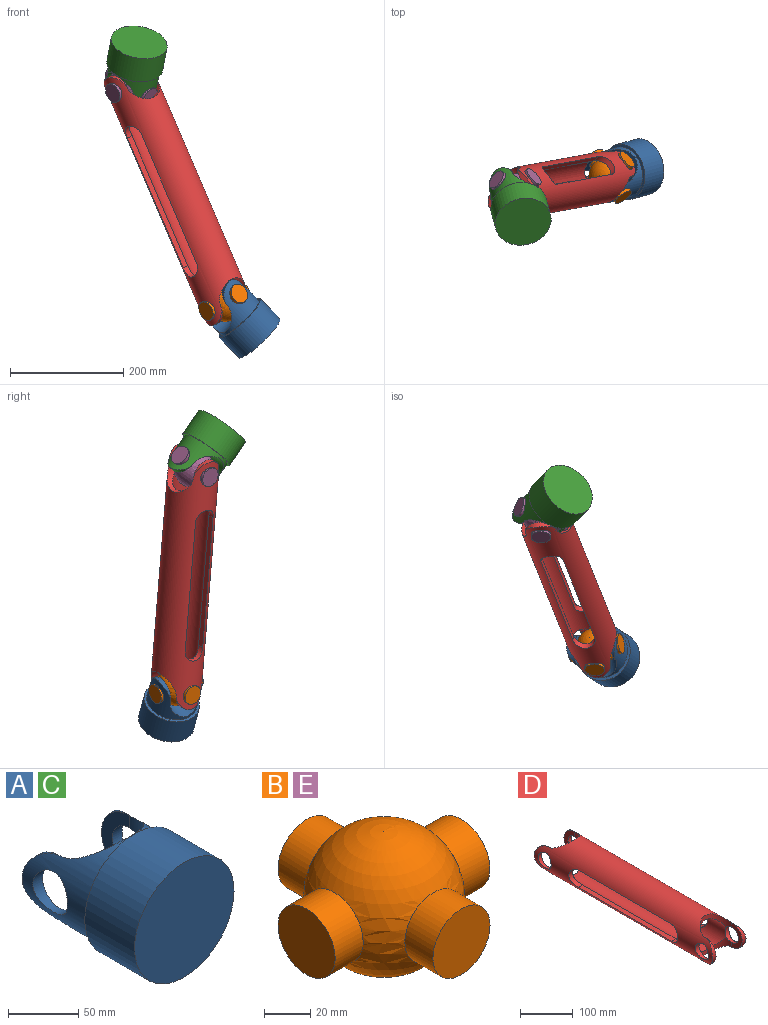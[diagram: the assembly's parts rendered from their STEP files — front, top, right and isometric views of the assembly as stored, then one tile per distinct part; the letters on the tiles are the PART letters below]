
ASSEMBLY  parts=5 mates=4
PART A: 11 faces, bbox 100x118.3x100 mm
  f0: cylinder r=45mm len=90mm, axis (0,-1,0), area 7768.4mm2, adj f4,f6,f7,f8,f9,f10
  f1: plane 56.57x28.28mm, normal (-1,0,0), area 775.6mm2, adj f6,f9,f10
  f2: plane 56.57x28.28mm, normal (1,0,0), area 775.6mm2, adj f6,f7,f8
  f3: cylinder r=50mm len=100mm, axis (0,-1,0), area 15708mm2, adj f4,f5
  f4: plane 100x100mm, normal (0,1,0), area 1492.3mm2, adj f0,f3
  f5: plane 100x100mm, normal (0,-1,0), area 7854mm2, adj f3
  f6: cylinder r=35mm len=90mm, axis (0,0,1), area 7167.4mm2, adj f0,f1,f2,f8,f10
  f7: cylinder r=28.28mm len=56.57mm, axis (1,0,0), area 458.2mm2, adj f0,f2
  f8: cylinder r=17.5mm len=35mm, axis (1,0,0), area 1033.1mm2, adj f0,f2,f6
  f9: cylinder r=28.28mm len=56.57mm, axis (1,0,0), area 458.1mm2, adj f0,f1
  f10: cylinder r=17.5mm len=35mm, axis (1,0,0), area 1033.8mm2, adj f0,f1,f6
PART B: 9 faces, bbox 95x95x70 mm
  f0: sphere r=35mm, area 11269mm2, adj f1,f4,f6,f7
  f1: cylinder r=17.5mm len=35mm, axis (0,1,0), area 1890mm2, adj f0,f2
  f2: plane 35x35mm, normal (0,1,0), area 962.1mm2, adj f1
  f3: plane 35x35mm, normal (0,-1,0), area 962.1mm2, adj f4
  f4: cylinder r=17.5mm len=35mm, axis (0,1,0), area 1890mm2, adj f0,f3
  f5: plane 35x35mm, normal (1,0,0), area 962.1mm2, adj f6
  f6: cylinder r=17.5mm len=35mm, axis (-1,0,0), area 1890mm2, adj f0,f5
  f7: cylinder r=17.5mm len=35mm, axis (-1,0,0), area 1890mm2, adj f0,f8
  f8: plane 35x35mm, normal (-1,0,0), area 962.1mm2, adj f7
PART C: same geometry as A
PART D: 26 faces, bbox 90x476.6x90 mm
  f0: cylinder r=45mm len=476.57mm, axis (0,1,0), area 88359.1mm2, adj f2,f3,f6,f7,f8,f9,f10,f11
  f1: cylinder r=35mm len=395.25mm, axis (0,1,0), area 57669.8mm2, adj f2,f3,f6,f7,f8,f9,f10,f11
  f2: cylinder r=35mm len=70mm, axis (0,0,1), area 1388.1mm2, adj f0,f1,f20,f21,f22,f23
  f3: cylinder r=35mm len=70mm, axis (0,0,1), area 1388.1mm2, adj f0,f1,f20,f21,f22,f23
  f4: plane 56.57x28.28mm, normal (-1,0,0), area 775.6mm2, adj f14,f15,f17,f19
  f5: plane 56.57x28.28mm, normal (1,0,0), area 775.6mm2, adj f14,f15,f16,f18
  f6: plane 250x11.59mm, normal (0,0,1), area 2897.1mm2, adj f0,f1,f7,f9
  f7: cylinder r=20mm len=40mm, axis (-1,0,0), area 675.4mm2, adj f0,f1,f6,f8
  f8: plane 250x11.59mm, normal (0,0,-1), area 2897.1mm2, adj f0,f1,f7,f9
  f9: cylinder r=20mm len=40mm, axis (-1,0,0), area 675.4mm2, adj f0,f1,f6,f8
  f10: cylinder r=20mm len=40mm, axis (-1,0,0), area 675.4mm2, adj f0,f1,f11,f13
  f11: plane 250x11.59mm, normal (0,0,-1), area 2897.1mm2, adj f0,f1,f10,f12
  f12: cylinder r=20mm len=40mm, axis (-1,0,0), area 675.4mm2, adj f0,f1,f11,f13
  f13: plane 250x11.59mm, normal (0,0,1), area 2897.1mm2, adj f0,f1,f10,f12
  f14: cylinder r=35mm len=70mm, axis (0,0,1), area 1388.1mm2, adj f0,f1,f4,f5,f16,f17
  f15: cylinder r=35mm len=70mm, axis (0,0,1), area 1388.1mm2, adj f0,f1,f4,f5,f16,f17
  f16: cylinder r=17.5mm len=35mm, axis (1,0,0), area 951.1mm2, adj f0,f1,f5,f14,f15
  f17: cylinder r=17.5mm len=35mm, axis (1,0,0), area 951.9mm2, adj f0,f1,f4,f14,f15
  f18: cylinder r=28.28mm len=56.57mm, axis (1,0,0), area 458.2mm2, adj f0,f5
  f19: cylinder r=28.28mm len=56.57mm, axis (1,0,0), area 458.1mm2, adj f0,f4
  f20: plane 56.57x28.28mm, normal (-1,0,0), area 775.6mm2, adj f2,f3,f23,f25
  f21: plane 56.57x28.28mm, normal (1,0,0), area 775.6mm2, adj f2,f3,f22,f24
  f22: cylinder r=17.5mm len=35mm, axis (1,0,0), area 951.9mm2, adj f0,f1,f2,f3,f21
  f23: cylinder r=17.5mm len=35mm, axis (1,0,0), area 951.1mm2, adj f0,f1,f2,f3,f20
  f24: cylinder r=28.28mm len=56.57mm, axis (1,0,0), area 458.1mm2, adj f0,f21
  f25: cylinder r=28.28mm len=56.57mm, axis (1,0,0), area 458.2mm2, adj f0,f20
PART E: same geometry as B
PLACE A rot(axis=(0.07,0.48,0.87),123.7deg) t=(-306.27,-21.69,-356.19)mm
PLACE B rot(axis=(-0.23,-0.55,0.8),47.2deg) t=(-367,-38.89,-292.04)mm
PLACE C rot(axis=(-0.12,-0.86,0.49),137.1deg) t=(-518.09,-119.98,166.32)mm fixed
PLACE D rot(axis=(0.85,0.13,0.51),95.2deg) t=(-547.68,-72.63,129.65)mm
PLACE E rot(axis=(-0.91,-0.4,-0.07),144.1deg) t=(-531.97,-69.7,92.98)mm
MATE revolute B.f1 <-> A.f7  axis (-0.55,0.78,-0.31) through (-347.85,-66.11,-281.21)mm
MATE revolute B.f6 <-> D.f22  axis (-0.7,-0.63,-0.35) through (-342.65,-16.91,-279.85)mm
MATE revolute C.f7 <-> E.f1  axis (0.71,-0.51,-0.49) through (-556.72,-51.72,109.98)mm
MATE revolute D.f16 <-> E.f6  axis (0.7,0.63,0.35) through (-556.31,-91.69,80.79)mm
